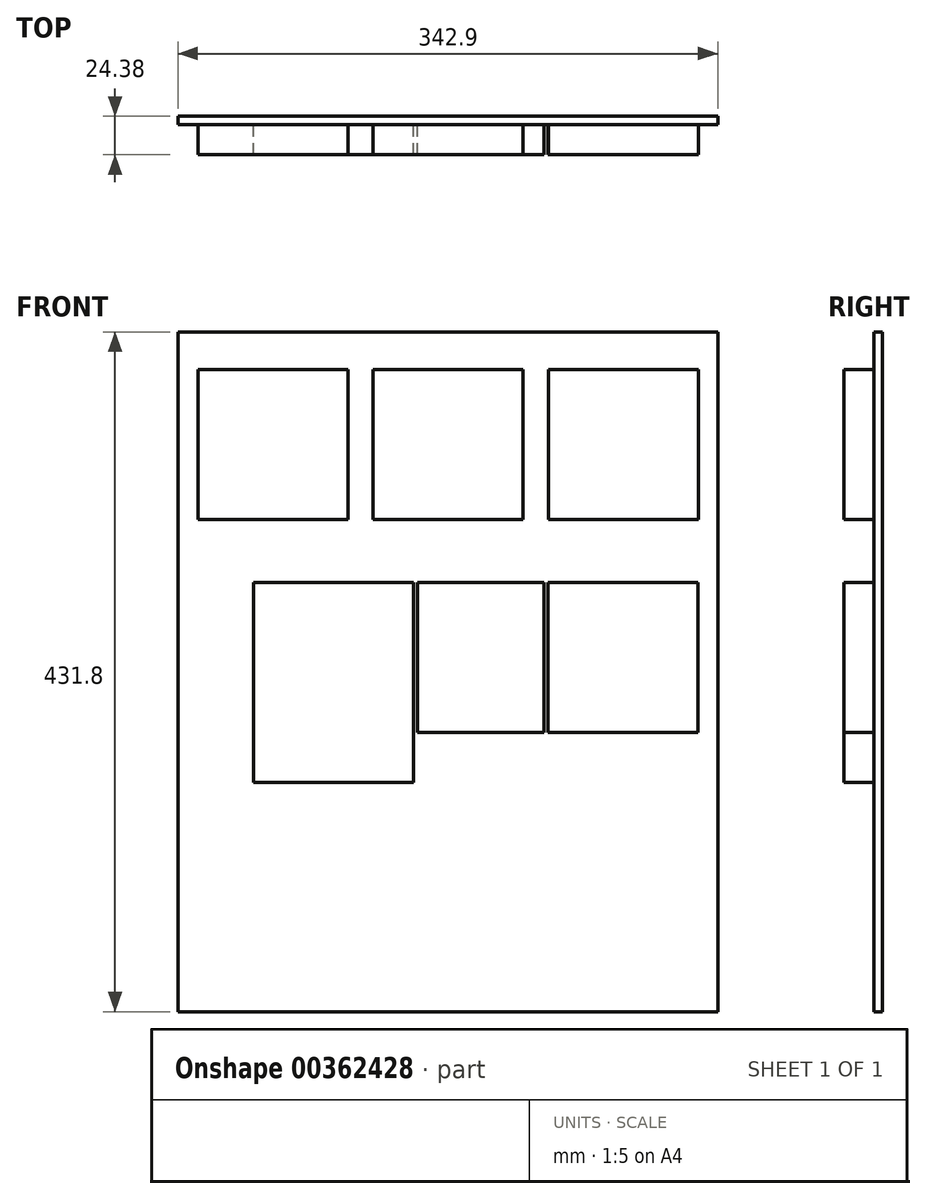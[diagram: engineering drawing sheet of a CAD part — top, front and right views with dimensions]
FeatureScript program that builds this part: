
annotation { "Feature Type Name" : "Feature", "Feature Type Description" : "" }
export const myFeature = defineFeature(function(context is Context, id is Id, definition is map)
    precondition{}
    {
        {
            var Q0;
            Q0=qCreatedBy(makeId("Front.planeOp"),FACE);
            var sketch = newSketch(context, id + "F0", { "sketchPlane" : qUnion([Q0])});
            skLineSegment(sketch, "E0.bottom", {"start": v(-197.75, 193.62) * mm, "end": v(145.15, 193.62) * mm});
            skLineSegment(sketch, "E0.top", {"start": v(-197.75, -238.18) * mm, "end": v(145.15, -238.18) * mm});
            skLineSegment(sketch, "E0.left", {"start": v(-197.75, 193.62) * mm, "end": v(-197.75, -238.18) * mm});
            skLineSegment(sketch, "E0.right", {"start": v(145.15, 193.62) * mm, "end": v(145.15, -238.18) * mm});
            skSolve(sketch);
        }
        {
            var Q0;
            Q0=makeQuery(id+"F0.imprint","IMPRINT",FACE,{"disambiguationData":[TD([[makeQuery(id+"F0.imprint","IMPRINT",EDGE,{"derivedFrom":sQuery(id+"F0.wireOp",EDGE,"E0.bottom")}),-1.0]])]});
            extrude(context, id + "F1", {"entities" : qUnion([Q0]), "depth" : 5.33 * mm});
        }
        {
            var Q0;
            Q0=makeQuery(id+"F1.opExtrude","CAP_FACE",FACE,{"disambiguationData":[OSD([sQuery(id+"F0.wireOp",EDGE,"E0.bottom"),sQuery(id+"F0.wireOp",EDGE,"E0.top"),sQuery(id+"F0.wireOp",EDGE,"E0.left"),sQuery(id+"F0.wireOp",EDGE,"E0.right")])],"isStart":false});
            var sketch = newSketch(context, id + "F2", { "sketchPlane" : qUnion([Q0])});
            skLineSegment(sketch, "E1.bottom", {"start": v(-185.05, 169.62) * mm, "end": v(-89.8, 169.62) * mm});
            skLineSegment(sketch, "E1.top", {"start": v(-185.05, 74.37) * mm, "end": v(-89.8, 74.37) * mm});
            skLineSegment(sketch, "E1.left", {"start": v(-185.05, 169.62) * mm, "end": v(-185.05, 74.37) * mm});
            skLineSegment(sketch, "E1.right", {"start": v(-89.8, 169.62) * mm, "end": v(-89.8, 74.37) * mm});
            skLineSegment(sketch, "E2.bottom", {"start": v(-73.8, 169.62) * mm, "end": v(21.45, 169.62) * mm});
            skLineSegment(sketch, "E2.top", {"start": v(-73.8, 74.37) * mm, "end": v(21.45, 74.37) * mm});
            skLineSegment(sketch, "E2.left", {"start": v(-73.8, 169.62) * mm, "end": v(-73.8, 74.37) * mm});
            skLineSegment(sketch, "E2.right", {"start": v(21.45, 169.62) * mm, "end": v(21.45, 74.37) * mm});
            skLineSegment(sketch, "E3.bottom", {"start": v(37.45, 169.62) * mm, "end": v(132.7, 169.62) * mm});
            skLineSegment(sketch, "E3.top", {"start": v(37.45, 74.37) * mm, "end": v(132.7, 74.37) * mm});
            skLineSegment(sketch, "E3.left", {"start": v(37.45, 169.62) * mm, "end": v(37.45, 74.37) * mm});
            skLineSegment(sketch, "E3.right", {"start": v(132.7, 169.62) * mm, "end": v(132.7, 74.37) * mm});
            skLineSegment(sketch, "E4.bottom", {"start": v(-149.75, 34.37) * mm, "end": v(-48.15, 34.37) * mm});
            skLineSegment(sketch, "E4.top", {"start": v(-149.75, -92.63) * mm, "end": v(-48.15, -92.63) * mm});
            skLineSegment(sketch, "E4.left", {"start": v(-149.75, 34.37) * mm, "end": v(-149.75, -92.63) * mm});
            skLineSegment(sketch, "E4.right", {"start": v(-48.15, 34.37) * mm, "end": v(-48.15, -92.63) * mm});
            skLineSegment(sketch, "E5.left", {"start": v(-48.15, 34.37) * mm, "end": v(-48.15, -60.88) * mm});
            skLineSegment(sketch, "E6.bottom", {"start": v(37.2, 34.37) * mm, "end": v(132.45, 34.37) * mm});
            skLineSegment(sketch, "E6.top", {"start": v(37.2, -60.88) * mm, "end": v(132.45, -60.88) * mm});
            skLineSegment(sketch, "E6.left", {"start": v(37.2, 34.37) * mm, "end": v(37.2, -60.88) * mm});
            skLineSegment(sketch, "E6.right", {"start": v(132.45, 34.37) * mm, "end": v(132.45, -60.88) * mm});
            skLineSegment(sketch, "E7.bottom", {"start": v(-45.61, 34.37) * mm, "end": v(34.66, 34.37) * mm});
            skLineSegment(sketch, "E7.top", {"start": v(-45.61, -60.88) * mm, "end": v(34.66, -60.88) * mm});
            skLineSegment(sketch, "E7.left", {"start": v(-45.61, 34.37) * mm, "end": v(-45.61, -60.88) * mm});
            skLineSegment(sketch, "E7.right", {"start": v(34.66, 34.37) * mm, "end": v(34.66, -60.88) * mm});
            skSolve(sketch);
        }
        {
            var Q0;
            Q0=makeQuery(id+"F2.imprint","IMPRINT",FACE,{"disambiguationData":[TD([[makeQuery(id+"F2.imprint","IMPRINT",EDGE,{"derivedFrom":sQuery(id+"F2.wireOp",EDGE,"E1.bottom")}),-1.0]])]});
            var Q1;
            Q1=makeQuery(id+"F2.imprint","IMPRINT",FACE,{"disambiguationData":[TD([[makeQuery(id+"F2.imprint","IMPRINT",EDGE,{"derivedFrom":sQuery(id+"F2.wireOp",EDGE,"E2.bottom")}),-1.0]])]});
            var Q2;
            Q2=makeQuery(id+"F2.imprint","IMPRINT",FACE,{"disambiguationData":[TD([[makeQuery(id+"F2.imprint","IMPRINT",EDGE,{"derivedFrom":sQuery(id+"F2.wireOp",EDGE,"E3.bottom")}),-1.0]])]});
            var Q3;
            Q3=makeQuery(id+"F2.imprint","IMPRINT",FACE,{"disambiguationData":[TD([[makeQuery(id+"F2.imprint","IMPRINT",EDGE,{"derivedFrom":sQuery(id+"F2.wireOp",EDGE,"E4.bottom")}),-1.0]])]});
            var Q4;
            Q4=makeQuery(id+"F2.imprint","IMPRINT",FACE,{"disambiguationData":[TD([[makeQuery(id+"F2.imprint","IMPRINT",EDGE,{"derivedFrom":sQuery(id+"F2.wireOp",EDGE,"tm915t4l-wwrN-Zizo-lA0P-x97mOZmAwLms.bottom")}),-1.0]])]});
            var Q5;
            {var subQ5=sQuery(id+"F2.wireOp",EDGE,"tm915t4l-wwrN-Zizo-lA0P-x97mOZmAwLms.left");Q5=makeQuery(id+"F2.imprint","IMPRINT",FACE,{"disambiguationData":[TD([[makeQuery(id+"F2.imprint","IMPRINT",EDGE,{"derivedFrom":subQ5}),-1.0]])]});}
            var Q6;
            Q6=makeQuery(id+"F2.imprint","IMPRINT",FACE,{"disambiguationData":[TD([[makeQuery(id+"F2.imprint","IMPRINT",EDGE,{"derivedFrom":sQuery(id+"F2.wireOp",EDGE,"E7.bottom")}),-1.0]])]});
            var Q7;
            Q7=makeQuery(id+"F2.imprint","IMPRINT",FACE,{"disambiguationData":[TD([[makeQuery(id+"F2.imprint","IMPRINT",EDGE,{"derivedFrom":sQuery(id+"F2.wireOp",EDGE,"E6.bottom")}),-1.0]])]});
            extrude(context, id + "F3", {"entities" : qUnion([Q0, Q1, Q2, Q3, Q4, Q5, Q6, Q7]), "operationType" : NewBodyOperationType.ADD, "depth" : 19.05 * mm});
        }
    });
